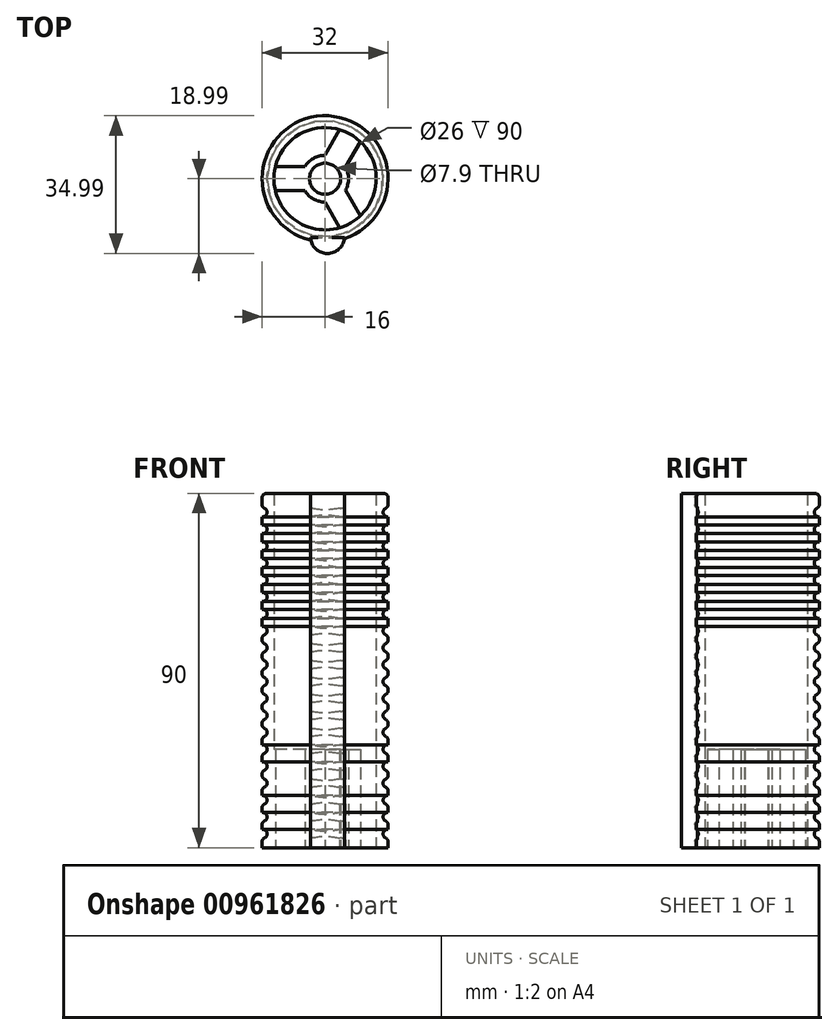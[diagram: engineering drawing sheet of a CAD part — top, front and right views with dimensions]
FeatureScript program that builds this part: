
annotation { "Feature Type Name" : "Feature", "Feature Type Description" : "" }
export const myFeature = defineFeature(function(context is Context, id is Id, definition is map)
    precondition{}
    {
        {
            var Q0;
            Q0=qCreatedBy(makeId("Top.planeOp"),FACE);
            var sketch = newSketch(context, id + "F0", { "sketchPlane" : qUnion([Q0])});
            skCircle(sketch, "E0", {"center": v(0, 0) * mm, "radius": 16 * mm});
            skCircle(sketch, "E1", {"center": v(0, 0) * mm, "radius": 3.95 * mm});
            skCircle(sketch, "E2.0", {"center": v(0, 0) * mm, "radius": 13 * mm});
            skCircle(sketch, "E3.0", {"center": v(0, 0) * mm, "radius": 5.95 * mm});
            skSolve(sketch);
        }
        {
            var Q0;
            Q0=makeQuery(id+"F0.imprint","IMPRINT",FACE,{"disambiguationData":[TD([[makeQuery(id+"F0.imprint","IMPRINT",EDGE,{"derivedFrom":sQuery(id+"F0.wireOp",EDGE,"E0")}),1.0]])]});
            extrude(context, id + "F1", {"entities" : qUnion([Q0]), "depth" : 90 * mm, "offsetDistance" : 25 * mm});
        }
        {
            var Q0;
            Q0=qCreatedBy(makeId("Top.planeOp"),FACE);
            var sketch = newSketch(context, id + "F2", { "sketchPlane" : qUnion([Q0])});
            skLineSegment(sketch, "E4.bottom", {"start": v(0, 0) * mm, "end": v(-14.5, 0) * mm});
            skLineSegment(sketch, "E4.top", {"start": v(0, 3.02) * mm, "end": v(-14.5, 3.02) * mm});
            skLineSegment(sketch, "E4.left", {"start": v(0, 0) * mm, "end": v(0, 3.02) * mm});
            skLineSegment(sketch, "E4.right", {"start": v(-14.5, 0) * mm, "end": v(-14.5, 3.02) * mm});
            skLineSegment(sketch, "E5.MirrorCS", {"start": v(0, 0) * mm, "end": v(0, -3.02) * mm});
            skLineSegment(sketch, "E6.MirrorCS", {"start": v(-14.5, 0) * mm, "end": v(-14.5, -3.02) * mm});
            skLineSegment(sketch, "E7.MirrorCS", {"start": v(0, -3.02) * mm, "end": v(-14.5, -3.02) * mm});
            skLineSegment(sketch, "E8.1.0", {"start": v(2.62, 1.51) * mm, "end": v(9.87, -11.05) * mm});
            skLineSegment(sketch, "E8.1.1", {"start": v(0, 0) * mm, "end": v(7.25, -12.56) * mm});
            skLineSegment(sketch, "E8.1.2", {"start": v(-2.62, -1.51) * mm, "end": v(4.64, -14.07) * mm});
            skLineSegment(sketch, "E8.1.3", {"start": v(7.25, -12.56) * mm, "end": v(4.64, -14.07) * mm});
            skLineSegment(sketch, "E8.1.4", {"start": v(0, 0) * mm, "end": v(2.62, 1.51) * mm});
            skLineSegment(sketch, "E8.1.5", {"start": v(7.25, -12.56) * mm, "end": v(9.87, -11.05) * mm});
            skLineSegment(sketch, "E8.1.6", {"start": v(0, 0) * mm, "end": v(-2.62, -1.51) * mm});
            skLineSegment(sketch, "E8.2.0", {"start": v(-2.62, 1.51) * mm, "end": v(4.64, 14.07) * mm});
            skLineSegment(sketch, "E8.2.1", {"start": v(0, 0) * mm, "end": v(7.25, 12.56) * mm});
            skLineSegment(sketch, "E8.2.2", {"start": v(2.62, -1.51) * mm, "end": v(9.87, 11.05) * mm});
            skLineSegment(sketch, "E8.2.3", {"start": v(7.25, 12.56) * mm, "end": v(9.87, 11.05) * mm});
            skLineSegment(sketch, "E8.2.4", {"start": v(0, 0) * mm, "end": v(-2.62, 1.51) * mm});
            skLineSegment(sketch, "E8.2.5", {"start": v(7.25, 12.56) * mm, "end": v(4.64, 14.07) * mm});
            skLineSegment(sketch, "E8.2.6", {"start": v(0, 0) * mm, "end": v(2.62, -1.51) * mm});
            skPoint(sketch, "E8.center", {"position": v(0, 0) * mm});
            skSolve(sketch);
        }
        {
            var Q0;
            Q0 = qSketchRegion(id + "F2", true);
            extrude(context, id + "F3", {"entities" : qUnion([Q0]), "operationType" : NewBodyOperationType.ADD, "depth" : 25 * mm, "offsetDistance" : 25 * mm});
        }
        {
            var Q0;
            Q0=makeQuery(id+"F0.imprint","IMPRINT",FACE,{"disambiguationData":[TD([[makeQuery(id+"F0.imprint","IMPRINT",EDGE,{"derivedFrom":sQuery(id+"F0.wireOp",EDGE,"E1")}),1.0]])]});
            var Q1;
            Q1=makeQuery(id+"F0.imprint","IMPRINT",FACE,{"disambiguationData":[TD([[makeQuery(id+"F0.imprint","IMPRINT",EDGE,{"derivedFrom":sQuery(id+"F0.wireOp",EDGE,"E1")}),-1.0]])]});
            extrude(context, id + "F4", {"entities" : qUnion([Q0, Q1]), "operationType" : NewBodyOperationType.ADD, "depth" : 25 * mm, "offsetDistance" : 25 * mm});
        }
        {
            var Q0;
            Q0=makeQuery(id+"F0.imprint","IMPRINT",FACE,{"disambiguationData":[TD([[makeQuery(id+"F0.imprint","IMPRINT",EDGE,{"derivedFrom":sQuery(id+"F0.wireOp",EDGE,"E1")}),1.0]])]});
            extrude(context, id + "F5", {"entities" : qUnion([Q0]), "operationType" : NewBodyOperationType.REMOVE, "depth" : 100.3 * mm, "offsetDistance" : 25 * mm});
        }
        {
            var Q0;
            Q0=qCreatedBy(makeId("Right.planeOp"),FACE);
            var sketch = newSketch(context, id + "F6", { "sketchPlane" : qUnion([Q0])});
            skLineSegment(sketch, "E9", {"start": v(0, 46.96) * mm, "end": v(0, 0) * mm, "construction": true});
            skSolve(sketch);
        }
        {
            var Q0;
            Q0=qCreatedBy(makeId("Front.planeOp"),FACE);
            var sketch = newSketch(context, id + "F7", { "sketchPlane" : qUnion([Q0])});
            skCircle(sketch, "E10", {"center": v(15.86, 3.52) * mm, "radius": 1.13 * mm});
            skCircle(sketch, "E11.0.1.0", {"center": v(15.86, 7.82) * mm, "radius": 1.13 * mm});
            skCircle(sketch, "E11.0.2.0", {"center": v(15.86, 12.12) * mm, "radius": 1.13 * mm});
            skCircle(sketch, "E11.0.3.0", {"center": v(15.86, 16.42) * mm, "radius": 1.13 * mm});
            skCircle(sketch, "E11.0.4.0", {"center": v(15.86, 20.72) * mm, "radius": 1.13 * mm});
            skCircle(sketch, "E11.0.5.0", {"center": v(15.86, 25.02) * mm, "radius": 1.13 * mm});
            skCircle(sketch, "E11.0.6.0", {"center": v(15.86, 29.32) * mm, "radius": 1.13 * mm});
            skCircle(sketch, "E11.0.7.0", {"center": v(15.86, 33.62) * mm, "radius": 1.13 * mm});
            skLineSegment(sketch, "E11.direction1", {"start": v(15.86, 3.52) * mm, "end": v(40.86, 3.52) * mm, "construction": true});
            skLineSegment(sketch, "E11.direction2", {"start": v(15.86, 3.52) * mm, "end": v(15.86, 7.82) * mm, "construction": true});
            skCircle(sketch, "E12.0.0.8", {"center": v(15.86, 37.92) * mm, "radius": 1.13 * mm});
            skCircle(sketch, "E12.0.0.9", {"center": v(15.86, 42.22) * mm, "radius": 1.13 * mm});
            skCircle(sketch, "E12.0.0.10", {"center": v(15.86, 46.52) * mm, "radius": 1.13 * mm});
            skCircle(sketch, "E13.0.0.11", {"center": v(15.86, 50.82) * mm, "radius": 1.13 * mm});
            skCircle(sketch, "E13.0.0.12", {"center": v(15.86, 55.12) * mm, "radius": 1.13 * mm});
            skCircle(sketch, "E14.0.0.13", {"center": v(15.86, 59.42) * mm, "radius": 1.13 * mm});
            skCircle(sketch, "E14.0.0.14", {"center": v(15.86, 63.72) * mm, "radius": 1.13 * mm});
            skCircle(sketch, "E14.0.0.15", {"center": v(15.86, 68.02) * mm, "radius": 1.13 * mm});
            skCircle(sketch, "E14.0.0.16", {"center": v(15.86, 72.32) * mm, "radius": 1.13 * mm});
            skCircle(sketch, "E14.0.0.17", {"center": v(15.86, 76.62) * mm, "radius": 1.13 * mm});
            skCircle(sketch, "E14.0.0.18", {"center": v(15.86, 80.92) * mm, "radius": 1.13 * mm});
            skCircle(sketch, "E14.0.0.19", {"center": v(15.86, 85.22) * mm, "radius": 1.13 * mm});
            skSolve(sketch);
        }
        {
            var Q0;
            Q0 = qSketchRegion(id + "F6", true);
            var Q1;
            Q1 = qSketchRegion(id + "F7", true);
            var Q2;
            Q2=sQuery(id+"F6.wireOp",EDGE,"E9");
            revolve(context, id + "F8", {"operationType" : NewBodyOperationType.REMOVE, "surfaceOperationType" : NewSurfaceOperationType.NEW, "entities" : qUnion([Q0, Q1]), "axis" : qUnion([Q2]), "revolveType" : RevolveType.FULL, "oppositeDirection" : true});
        }
        {
            var Q0;
            {var subQ0=sQuery(id+"F0.wireOp",EDGE,"E0");Q0=makeQuery(id+"F8.boolean.opBoolean","SPLIT",FACE,{"disambiguationData":[TD([makeQuery(id+"F1.opExtrude","CAP_FACE",FACE,{"disambiguationData":[OSD([subQ0,sQuery(id+"F0.wireOp",EDGE,"E2.0")])],"isStart":false}),makeQuery(id+"F3.opExtrude","CAP_FACE",FACE,{"disambiguationData":[OSD([sQuery(id+"F2.wireOp",EDGE,"E4.top"),sQuery(id+"F2.wireOp",EDGE,"E4.right"),sQuery(id+"F2.wireOp",EDGE,"E6.MirrorCS"),sQuery(id+"F2.wireOp",EDGE,"E7.MirrorCS"),sQuery(id+"F2.wireOp",EDGE,"E8.1.0"),sQuery(id+"F2.wireOp",EDGE,"E8.1.2"),sQuery(id+"F2.wireOp",EDGE,"E8.1.3"),sQuery(id+"F2.wireOp",EDGE,"E8.1.5"),sQuery(id+"F2.wireOp",EDGE,"E8.2.0"),sQuery(id+"F2.wireOp",EDGE,"E8.2.2"),sQuery(id+"F2.wireOp",EDGE,"E8.2.3"),sQuery(id+"F2.wireOp",EDGE,"E8.2.5")])],"isStart":false}),makeQuery(id+"F4.opExtrude","CAP_FACE",FACE,{"disambiguationData":[OSD([sQuery(id+"F0.wireOp",EDGE,"E3.0")])],"isStart":false}),makeQuery(id+"F8.opRevolve","SWEPT_FACE",FACE,{"disambiguationData":[OSD([sQuery(id+"F7.wireOp",EDGE,"E11.0.7.0")])]})])],"derivedFrom":makeQuery(id+"F1.opExtrude","SWEPT_FACE",FACE,{"disambiguationData":[OSD([subQ0])]})});}
            var Q1;
            Q1=makeQuery(id+"F8.boolean.opBoolean","INTERSECT",EDGE,{"disambiguationData":[OD(1.0)],"derivedFrom":[makeQuery(id+"F1.opExtrude","SWEPT_FACE",FACE,{"disambiguationData":[OSD([sQuery(id+"F0.wireOp",EDGE,"E0")])]}),makeQuery(id+"F8.opRevolve","SWEPT_FACE",FACE,{"disambiguationData":[OSD([sQuery(id+"F7.wireOp",EDGE,"E11.0.7.0")])]})]});
            var Q2;
            Q2=makeQuery(id+"F8.boolean.opBoolean","INTERSECT",EDGE,{"disambiguationData":[OD(0.0)],"derivedFrom":[makeQuery(id+"F1.opExtrude","SWEPT_FACE",FACE,{"disambiguationData":[OSD([sQuery(id+"F0.wireOp",EDGE,"E0")])]}),makeQuery(id+"F8.opRevolve","SWEPT_FACE",FACE,{"disambiguationData":[OSD([sQuery(id+"F7.wireOp",EDGE,"E11.0.6.0")])]})]});
            var Q3;
            Q3=makeQuery(id+"F8.boolean.opBoolean","INTERSECT",EDGE,{"disambiguationData":[OD(0.0)],"derivedFrom":[makeQuery(id+"F1.opExtrude","SWEPT_FACE",FACE,{"disambiguationData":[OSD([sQuery(id+"F0.wireOp",EDGE,"E0")])]}),makeQuery(id+"F8.opRevolve","SWEPT_FACE",FACE,{"disambiguationData":[OSD([sQuery(id+"F7.wireOp",EDGE,"E11.0.5.0")])]})]});
            var Q4;
            Q4=makeQuery(id+"F8.boolean.opBoolean","SPLIT",FACE,{"disambiguationData":[TD([makeQuery(id+"F8.opRevolve","SWEPT_FACE",FACE,{"disambiguationData":[OSD([sQuery(id+"F7.wireOp",EDGE,"E11.0.3.0")])]}),makeQuery(id+"F8.opRevolve","SWEPT_FACE",FACE,{"disambiguationData":[OSD([sQuery(id+"F7.wireOp",EDGE,"E11.0.4.0")])]})])],"derivedFrom":makeQuery(id+"F1.opExtrude","SWEPT_FACE",FACE,{"disambiguationData":[OSD([sQuery(id+"F0.wireOp",EDGE,"E0")])]})});
            var Q5;
            Q5=makeQuery(id+"F8.boolean.opBoolean","INTERSECT",EDGE,{"disambiguationData":[OD(0.0)],"derivedFrom":[makeQuery(id+"F1.opExtrude","SWEPT_FACE",FACE,{"disambiguationData":[OSD([sQuery(id+"F0.wireOp",EDGE,"E0")])]}),makeQuery(id+"F8.opRevolve","SWEPT_FACE",FACE,{"disambiguationData":[OSD([sQuery(id+"F7.wireOp",EDGE,"E11.0.3.0")])]})]});
            var Q6;
            Q6=makeQuery(id+"F8.boolean.opBoolean","INTERSECT",EDGE,{"disambiguationData":[OD(0.0)],"derivedFrom":[makeQuery(id+"F1.opExtrude","SWEPT_FACE",FACE,{"disambiguationData":[OSD([sQuery(id+"F0.wireOp",EDGE,"E0")])]}),makeQuery(id+"F8.opRevolve","SWEPT_FACE",FACE,{"disambiguationData":[OSD([sQuery(id+"F7.wireOp",EDGE,"E11.0.2.0")])]})]});
            var Q7;
            Q7=makeQuery(id+"F8.boolean.opBoolean","INTERSECT",EDGE,{"disambiguationData":[OD(0.0)],"derivedFrom":[makeQuery(id+"F1.opExtrude","SWEPT_FACE",FACE,{"disambiguationData":[OSD([sQuery(id+"F0.wireOp",EDGE,"E0")])]}),makeQuery(id+"F8.opRevolve","SWEPT_FACE",FACE,{"disambiguationData":[OSD([sQuery(id+"F7.wireOp",EDGE,"E11.0.1.0")])]})]});
            var Q8;
            Q8=makeQuery(id+"F8.boolean.opBoolean","INTERSECT",EDGE,{"disambiguationData":[OD(0.0)],"derivedFrom":[makeQuery(id+"F1.opExtrude","SWEPT_FACE",FACE,{"disambiguationData":[OSD([sQuery(id+"F0.wireOp",EDGE,"E0")])]}),makeQuery(id+"F8.opRevolve","SWEPT_FACE",FACE,{"disambiguationData":[OSD([sQuery(id+"F7.wireOp",EDGE,"E10")])]})]});
            var Q9;
            Q9=makeQuery(id+"F8.boolean.opBoolean","SPLIT",FACE,{"disambiguationData":[TD([makeQuery(id+"F8.opRevolve","SWEPT_FACE",FACE,{"disambiguationData":[OSD([sQuery(id+"F7.wireOp",EDGE,"E12.0.0.8")])]}),makeQuery(id+"F8.opRevolve","SWEPT_FACE",FACE,{"disambiguationData":[OSD([sQuery(id+"F7.wireOp",EDGE,"E12.0.0.9")])]})])],"derivedFrom":makeQuery(id+"F1.opExtrude","SWEPT_FACE",FACE,{"disambiguationData":[OSD([sQuery(id+"F0.wireOp",EDGE,"E0")])]})});
            var Q10;
            Q10=makeQuery(id+"F8.boolean.opBoolean","SPLIT",FACE,{"disambiguationData":[TD([makeQuery(id+"F8.opRevolve","SWEPT_FACE",FACE,{"disambiguationData":[OSD([sQuery(id+"F7.wireOp",EDGE,"E12.0.0.9")])]}),makeQuery(id+"F8.opRevolve","SWEPT_FACE",FACE,{"disambiguationData":[OSD([sQuery(id+"F7.wireOp",EDGE,"E12.0.0.10")])]})])],"derivedFrom":makeQuery(id+"F1.opExtrude","SWEPT_FACE",FACE,{"disambiguationData":[OSD([sQuery(id+"F0.wireOp",EDGE,"E0")])]})});
            var Q11;
            Q11=makeQuery(id+"F8.boolean.opBoolean","SPLIT",FACE,{"disambiguationData":[TD([makeQuery(id+"F8.opRevolve","SWEPT_FACE",FACE,{"disambiguationData":[OSD([sQuery(id+"F7.wireOp",EDGE,"E12.0.0.10")])]}),makeQuery(id+"F8.opRevolve","SWEPT_FACE",FACE,{"disambiguationData":[OSD([sQuery(id+"F7.wireOp",EDGE,"E13.0.0.11")])]})])],"derivedFrom":makeQuery(id+"F1.opExtrude","SWEPT_FACE",FACE,{"disambiguationData":[OSD([sQuery(id+"F0.wireOp",EDGE,"E0")])]})});
            var Q12;
            Q12=makeQuery(id+"F8.boolean.opBoolean","SPLIT",FACE,{"disambiguationData":[TD([makeQuery(id+"F8.opRevolve","SWEPT_FACE",FACE,{"disambiguationData":[OSD([sQuery(id+"F7.wireOp",EDGE,"E13.0.0.11")])]}),makeQuery(id+"F8.opRevolve","SWEPT_FACE",FACE,{"disambiguationData":[OSD([sQuery(id+"F7.wireOp",EDGE,"E13.0.0.12")])]})])],"derivedFrom":makeQuery(id+"F1.opExtrude","SWEPT_FACE",FACE,{"disambiguationData":[OSD([sQuery(id+"F0.wireOp",EDGE,"E0")])]})});
            fillet(context, id + "F9", {"entities" : qUnion([Q0, Q1, Q2, Q3, Q4, Q5, Q6, Q7, Q8, Q9, Q10, Q11, Q12]), "radius" : 1 * mm, "tangentPropagation" : true, "allowEdgeOverflow" : false});
        }
        {
            var Q0;
            Q0=qCreatedBy(makeId("Top.planeOp"),FACE);
            var sketch = newSketch(context, id + "F10", { "sketchPlane" : qUnion([Q0])});
            skArc(sketch, "E15", {"start": v(-3.74, -14.9) * mm, "mid": v(0.6, -18.99) * mm, "end": v(4.95, -14.9) * mm});
            skLineSegment(sketch, "E16", {"start": v(-3.74, -14.9) * mm, "end": v(4.95, -14.9) * mm});
            skSolve(sketch);
        }
        {
            var Q0;
            Q0=makeQuery(id+"F10.imprint","IMPRINT",FACE,{"disambiguationData":[TD([[makeQuery(id+"F10.imprint","IMPRINT",EDGE,{"derivedFrom":sQuery(id+"F10.wireOp",EDGE,"E15")}),1.0]])]});
            var Q1;
            Q1=makeQuery(id+"F1.opExtrude","CAP_FACE",FACE,{"disambiguationData":[OSD([sQuery(id+"F0.wireOp",EDGE,"E0"),sQuery(id+"F0.wireOp",EDGE,"E2.0")])],"isStart":false});
            extrude(context, id + "F11", {"entities" : qUnion([Q0]), "operationType" : NewBodyOperationType.ADD, "endBound" : BoundingType.UP_TO_SURFACE, "depth" : 25 * mm, "endBoundEntityFace" : qUnion([Q1]), "offsetDistance" : 25 * mm});
        }
    });
